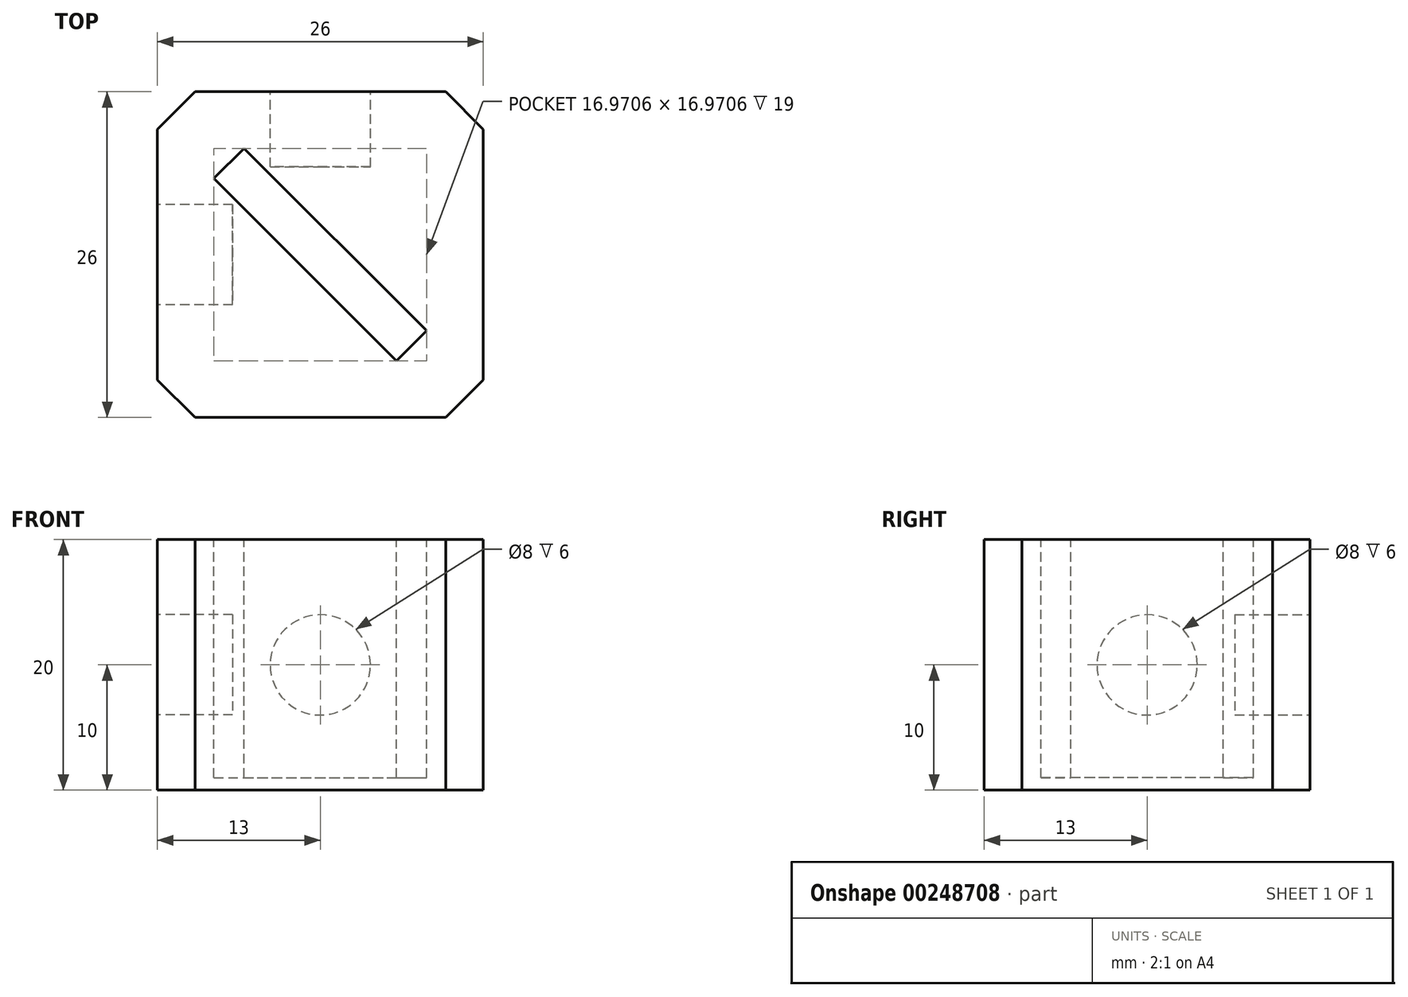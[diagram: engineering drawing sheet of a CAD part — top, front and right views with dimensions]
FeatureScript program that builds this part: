
annotation { "Feature Type Name" : "Feature", "Feature Type Description" : "" }
export const myFeature = defineFeature(function(context is Context, id is Id, definition is map)
    precondition{}
    {
        {
            var Q0;
            Q0=qCreatedBy(makeId("Top.planeOp"),FACE);
            var sketch = newSketch(context, id + "F0", { "sketchPlane" : qUnion([Q0])});
            skLineSegment(sketch, "E0.bottom", {"start": v(-13, 13) * mm, "end": v(13, 13) * mm});
            skLineSegment(sketch, "E0.top", {"start": v(-13, -13) * mm, "end": v(13, -13) * mm});
            skLineSegment(sketch, "E0.left", {"start": v(-13, 13) * mm, "end": v(-13, -13) * mm});
            skLineSegment(sketch, "E0.right", {"start": v(13, 13) * mm, "end": v(13, -13) * mm});
            skPoint(sketch, "E0.middle", {"position": v(0, 0) * mm});
            skSolve(sketch);
        }
        {
            var Q0;
            Q0 = qSketchRegion(id + "F0", true);
            extrude(context, id + "F1", {"entities" : qUnion([Q0]), "depth" : 20 * mm});
        }
        {
            var Q0;
            Q0=makeQuery(id+"F1.opExtrude","SWEPT_EDGE",EDGE,{"disambiguationData":[OSD([sQuery(id+"F0.wireOp",EDGE,"E0.top"),sQuery(id+"F0.wireOp",EDGE,"E0.left")])]});
            var Q1;
            Q1=makeQuery(id+"F1.opExtrude","SWEPT_EDGE",EDGE,{"disambiguationData":[OSD([sQuery(id+"F0.wireOp",EDGE,"E0.top"),sQuery(id+"F0.wireOp",EDGE,"E0.right")])]});
            var Q2;
            Q2=makeQuery(id+"F1.opExtrude","SWEPT_EDGE",EDGE,{"disambiguationData":[OSD([sQuery(id+"F0.wireOp",EDGE,"E0.bottom"),sQuery(id+"F0.wireOp",EDGE,"E0.right")])]});
            var Q3;
            Q3=makeQuery(id+"F1.opExtrude","SWEPT_EDGE",EDGE,{"disambiguationData":[OSD([sQuery(id+"F0.wireOp",EDGE,"E0.bottom"),sQuery(id+"F0.wireOp",EDGE,"E0.left")])]});
            chamfer(context, id + "F2", {"entities" : qUnion([Q0, Q1, Q2, Q3]), "width" : 3 * mm, "tangentPropagation" : true});
        }
        {
            var Q0;
            Q0=makeQuery(id+"F1.opExtrude","CAP_FACE",FACE,{"disambiguationData":[OSD([sQuery(id+"F0.wireOp",EDGE,"E0.bottom"),sQuery(id+"F0.wireOp",EDGE,"E0.top"),sQuery(id+"F0.wireOp",EDGE,"E0.left"),sQuery(id+"F0.wireOp",EDGE,"E0.right")])],"isStart":false});
            var sketch = newSketch(context, id + "F3", { "sketchPlane" : qUnion([Q0])});
            skLineSegment(sketch, "E1", {"start": v(-11.5, 11.5) * mm, "end": v(11.5, -11.5) * mm});
            skLineSegment(sketch, "E2", {"start": v(-10.6, 13) * mm, "end": v(13, -10.6) * mm});
            skLineSegment(sketch, "E3", {"start": v(-13, 10.6) * mm, "end": v(10.6, -13) * mm});
            skLineSegment(sketch, "E4", {"start": v(-8.49, 6.08) * mm, "end": v(-6.08, 8.49) * mm});
            skLineSegment(sketch, "E5", {"start": v(6.08, -8.49) * mm, "end": v(8.49, -6.08) * mm});
            skLineSegment(sketch, "E6", {"start": v(0, 0) * mm, "end": v(-1.2, -1.2) * mm});
            skSolve(sketch);
        }
        {
            var Q0;
            Q0 = qSketchRegion(id + "F3", true);
            extrude(context, id + "F4", {"entities" : qUnion([Q0]), "operationType" : NewBodyOperationType.REMOVE, "oppositeDirection" : true, "depth" : 19 * mm});
        }
        {
            var Q0;
            Q0=makeQuery(id+"F1.opExtrude","SWEPT_FACE",FACE,{"disambiguationData":[OSD([sQuery(id+"F0.wireOp",EDGE,"E0.left")])]});
            var sketch = newSketch(context, id + "F5", { "sketchPlane" : qUnion([Q0])});
            skCircle(sketch, "E7", {"center": v(0, 10) * mm, "radius": 4 * mm});
            skPoint(sketch, "E7.centerSnap0", {"position": v(10, 10) * mm});
            skPoint(sketch, "E7.centerSnap1", {"position": v(0, 20) * mm});
            skSolve(sketch);
        }
        {
            var Q0;
            Q0 = qSketchRegion(id + "F5", true);
            extrude(context, id + "F6", {"entities" : qUnion([Q0]), "operationType" : NewBodyOperationType.REMOVE, "oppositeDirection" : true, "depth" : 6 * mm});
        }
        {
            var Q0;
            Q0=makeQuery(id+"F1.opExtrude","SWEPT_FACE",FACE,{"disambiguationData":[OSD([sQuery(id+"F0.wireOp",EDGE,"E0.bottom")])]});
            var sketch = newSketch(context, id + "F7", { "sketchPlane" : qUnion([Q0])});
            skCircle(sketch, "E8", {"center": v(0, 10) * mm, "radius": 4 * mm});
            skPoint(sketch, "E8.centerSnap0", {"position": v(10, 10) * mm});
            skPoint(sketch, "E8.centerSnap1", {"position": v(0, 20) * mm});
            skSolve(sketch);
        }
        {
            var Q0;
            Q0 = qSketchRegion(id + "F7", true);
            extrude(context, id + "F8", {"entities" : qUnion([Q0]), "operationType" : NewBodyOperationType.REMOVE, "oppositeDirection" : true, "depth" : 6 * mm});
        }
    });
